# Revit family: Gleitschlitten Typ B, höhe h=150mm, Ø610 bis Ø813mm, m.D
name_source: partatom
category: HLS-Bauteile
revit_build: Autodesk Revit 2018 (Build: 20190510_1515(x64)
units: mm (PartAtom-declared; Revit-internal decimal feet)

## family parameters
Arbeitsebenenbasiert = Ja
Beim Laden mit Abzugskörper schneiden = Nein
Bemaßung runder Anschluss = Durchmesser verwenden
Gemeinsam genutzt = Ja
Immer vertikal = Nein
Klassifizierung = Keine
Raumberechnungspunkt = Nein
Teiletyp = Normal

## types (3) — shared parameters
Baustoffklasse = B2
Breite Schellenband = 70 mm
Dämmstärke = 6 mm  [stored 0.019685 ft]
Fabrikat = MEFA
Höhe Schießnaht RS = 100 mm  [stored 0.328084 ft]
Kurztext1 = Gleitschlitten B 70 x 10 mm
Mengeneinheit = St
Schalldämmeinlage = Gummi EPDM
Sicherheitsfaktor = 1.54
Stärke Schellenband = 10 mm
Verschluss = Schraube + Mutter
Verschluss-Schraube = M20
Vorgabe-Ansicht = 1219 mm
max. Temperaturbeständigkeit = 100 °C
vpe = 1

## per-type parameters (varying)
| type | A (Breite) | Abstand RS AK | Achshöhe | Achshöhe _ | Artikelnummer | Breite Unterbau | EAN | Flachmaterial | Gewicht | Gewicht pro Bauteil | Kurztext2 | L | Länge Unterbau | RS Ø610 bis Ø813 | Rohraußendurchmesser | Stärke Material | TL Platte |
| Gleitschlitten TypB, h=150mm, m.D., Ø610mm | 289 mm  [stored 0.948163 ft] | 370 mm  [stored 1.21391 ft] | 455 mm | 455 mm | 110bfb0610 | 438 mm | 4250928462343 | Flachmaterial nach DIN (70-8 und 70-10) : für Ø610 | 47.18 kg | 47.18 kg | 610 mm EPDM fsv | 390 mm  [stored 1.27953 ft] | 390 mm | Rohrschelle Titan HD, Gummi, 30 Grad, Ø610 bis Ø813, ok : für Ø610 | 610 mm  [stored 2.00131 ft] | 10 mm  [stored 0.0328084 ft] | TL-Fuß für Gleitschl.2Lo.14 für 70-10 : TL für 10-390-175 |
| Gleitschlitten TypB, h=150mm, m.D., Ø711mm | 313 mm  [stored 1.0269 ft] | 370 mm  [stored 1.21391 ft] | 557 mm | 506 mm  [stored 1.6601 ft] | 110bfb0711 | 509 mm | 4250928462350 | Flachmaterial nach DIN (70-8 und 70-10) : für Ø711 | 51.64 kg | 51.64 kg | 813 mm EPDM fsv | 390 mm  [stored 1.27953 ft] | 470 mm | Rohrschelle Titan HD, Gummi, 30 Grad, Ø610 bis Ø813, ok : für Ø711 | 813 mm | 12 mm  [stored 0.0393701 ft] | TL-Fuß für Gleitschl.2Lo.14 für 70-10 : TL für 10-390-175 |
| Gleitschlitten TypB, h=150mm, m.D., Ø813mm | 357 mm  [stored 1.17126 ft] | 450 mm  [stored 1.47638 ft] | 506 mm | 557 mm  [stored 1.82743 ft] | 110bfb0813 | 464 mm | 4250928462367 | Flachmaterial nach DIN (70-8 und 70-10) : für Ø813 | 63.71 kg | 63.71 kg | 711 mm EPDM fsv | 470 mm  [stored 1.54199 ft] | 390 mm | Rohrschelle Titan HD, Gummi, 30 Grad, Ø610 bis Ø813, ok : für Ø813 | 711 mm  [stored 2.33268 ft] | 10 mm  [stored 0.0328084 ft] | TL-Fuß für Gleitschl.2Lo.14 für 70-10 : TL für 12-470-180 |

note: [stored X ft] marks values corroborated as IEEE doubles in the binary element streams (Revit-internal decimal feet)

## geometry (parser evidence)
native form markers: Sweep x9
no freeform markers — native parametric forms only
